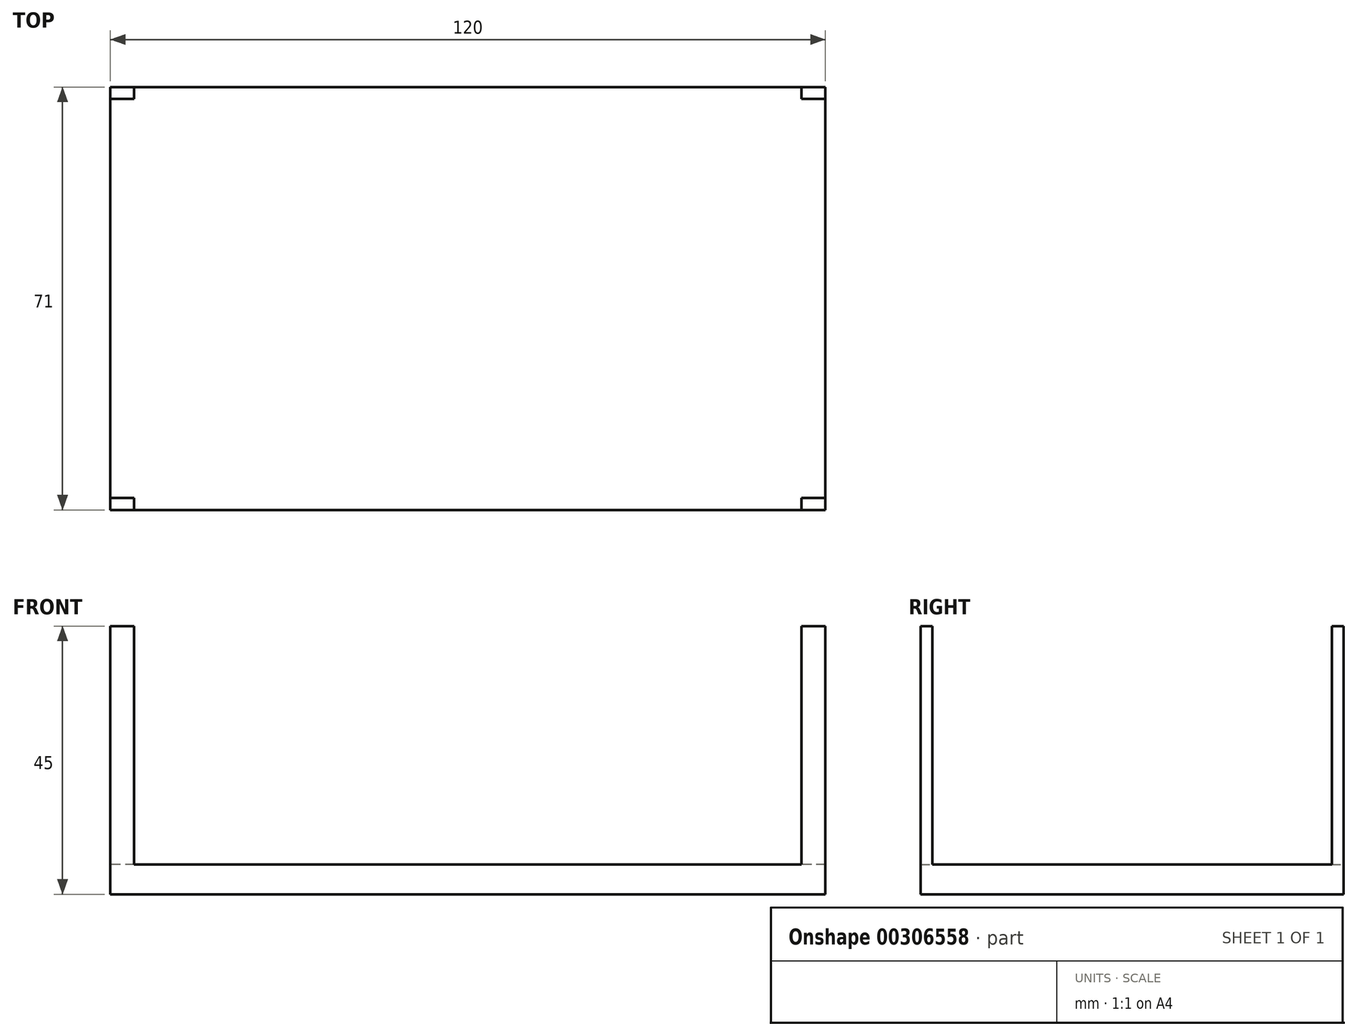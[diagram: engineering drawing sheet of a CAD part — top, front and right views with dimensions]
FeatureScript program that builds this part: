
annotation { "Feature Type Name" : "Feature", "Feature Type Description" : "" }
export const myFeature = defineFeature(function(context is Context, id is Id, definition is map)
    precondition{}
    {
        {
            var Q0;
            Q0=qCreatedBy(makeId("Front.planeOp"),FACE);
            var sketch = newSketch(context, id + "F0", { "sketchPlane" : qUnion([Q0])});
            skLineSegment(sketch, "E0.bottom", {"start": v(0, 0) * mm, "end": v(40, 0) * mm});
            skLineSegment(sketch, "E0.top", {"start": v(0, -400) * mm, "end": v(40, -400) * mm});
            skLineSegment(sketch, "E0.left", {"start": v(0, 0) * mm, "end": v(0, -400) * mm});
            skLineSegment(sketch, "E0.right", {"start": v(40, 0) * mm, "end": v(40, -400) * mm});
            skLineSegment(sketch, "E1.bottom", {"start": v(0, 0) * mm, "end": v(1200, 0) * mm});
            skLineSegment(sketch, "E1.top", {"start": v(0, 50) * mm, "end": v(1200, 50) * mm});
            skLineSegment(sketch, "E1.left", {"start": v(0, 0) * mm, "end": v(0, 50) * mm});
            skLineSegment(sketch, "E1.right", {"start": v(1200, 0) * mm, "end": v(1200, 50) * mm});
            skLineSegment(sketch, "E2.bottom", {"start": v(1200, 0) * mm, "end": v(1160, 0) * mm});
            skLineSegment(sketch, "E2.top", {"start": v(1200, -400) * mm, "end": v(1160, -400) * mm});
            skLineSegment(sketch, "E2.left", {"start": v(1200, 0) * mm, "end": v(1200, -400) * mm});
            skLineSegment(sketch, "E2.right", {"start": v(1160, 0) * mm, "end": v(1160, -400) * mm});
            skSolve(sketch);
        }
        {
            var Q0;
            Q0=qSketchRegion(id+"F0",true);
            extrude(context, id + "F1", {"entities" : qUnion([Q0]), "depth" : 710 * mm});
        }
        {
            var Q0;
            Q0=makeQuery(id+"F1.opExtrude","SWEPT_FACE",FACE,{"disambiguationData":[OSD([sQuery(id+"F0.wireOp",EDGE,"E1.right"),sQuery(id+"F0.wireOp",EDGE,"E2.left")])]});
            var sketch = newSketch(context, id + "F2", { "sketchPlane" : qUnion([Q0])});
            skLineSegment(sketch, "E3.bottom", {"start": v(-690, 0) * mm, "end": v(-20, 0) * mm});
            skLineSegment(sketch, "E3.top", {"start": v(-690, -400) * mm, "end": v(-20, -400) * mm});
            skLineSegment(sketch, "E3.left", {"start": v(-690, 0) * mm, "end": v(-690, -400) * mm});
            skLineSegment(sketch, "E3.right", {"start": v(-20, 0) * mm, "end": v(-20, -400) * mm});
            skSolve(sketch);
        }
        {
            var Q0;
            Q0=qSketchRegion(id+"F2",true);
            extrude(context, id + "F3", {"entities" : qUnion([Q0]), "operationType" : NewBodyOperationType.REMOVE, "oppositeDirection" : true, "depth" : 1250 * mm});
        }
        {
            var Q0;
            Q0=makeQuery(id+"F1.opExtrude","SWEPT_BODY",BODY,{"disambiguationData":[OSD([sQuery(id+"F0.wireOp",EDGE,"E0.top"),sQuery(id+"F0.wireOp",EDGE,"E0.left"),sQuery(id+"F0.wireOp",EDGE,"E0.right"),sQuery(id+"F0.wireOp",EDGE,"E1.bottom"),sQuery(id+"F0.wireOp",EDGE,"E1.top"),sQuery(id+"F0.wireOp",EDGE,"E1.left"),sQuery(id+"F0.wireOp",EDGE,"E1.right"),sQuery(id+"F0.wireOp",EDGE,"E2.top"),sQuery(id+"F0.wireOp",EDGE,"E2.left"),sQuery(id+"F0.wireOp",EDGE,"E2.right")])]});
            var Q1;
            Q1=qCreatedBy(makeId("Origin.pointOp"),VERTEX);
            transform(context, id + "F4", {"entities" : qUnion([Q0]), "transformType" : TransformType.SCALE_UNIFORMLY, "scale" : 0.1, "scalePoint" : qUnion([Q1]), "makeCopy" : false});
        }
        {
            var Q0;
            Q0=makeQuery(id+"F1.opExtrude","SWEPT_BODY",BODY,{"disambiguationData":[OSD([sQuery(id+"F0.wireOp",EDGE,"E0.top"),sQuery(id+"F0.wireOp",EDGE,"E0.left"),sQuery(id+"F0.wireOp",EDGE,"E0.right"),sQuery(id+"F0.wireOp",EDGE,"E1.bottom"),sQuery(id+"F0.wireOp",EDGE,"E1.top"),sQuery(id+"F0.wireOp",EDGE,"E1.left"),sQuery(id+"F0.wireOp",EDGE,"E1.right"),sQuery(id+"F0.wireOp",EDGE,"E2.top"),sQuery(id+"F0.wireOp",EDGE,"E2.left"),sQuery(id+"F0.wireOp",EDGE,"E2.right")])]});
            var Q1;
            Q1=makeQuery(id+"F1.opExtrude","SWEPT_EDGE",EDGE,{"disambiguationData":[OSD([sQuery(id+"F0.wireOp",EDGE,"E1.top"),sQuery(id+"F0.wireOp",EDGE,"E1.left")])]});
            transform(context, id + "F5", {"entities" : qUnion([Q0]), "transformType" : TransformType.ROTATION, "transformAxis" : qUnion([Q1]), "angle" : 180 * degree, "makeCopy" : false});
        }
    });
